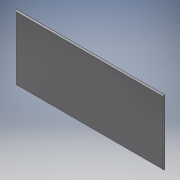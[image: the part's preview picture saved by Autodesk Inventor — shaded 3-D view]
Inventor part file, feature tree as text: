
AUTODESK INVENTOR PART (.ipt)
format: ipt  version: 2018 (Build 220112000, 112)  size: 105,472 bytes
history: native  units: in
note: dims shown in document units (in); Inventor stores cm internally (conversion verified against a paired STEP export)
features: other x3, extrude x2, sketch x2, fillet x1, reference x1, projected_geometry x1
ambient origin geometry x8: Origin, YZ Plane, XZ Plane, XY Plane, X Axis, Y Axis, Z Axis, Center Point
bodies: Solid1 (feature_tree)
feature tree (10):
  extrude  "Extrusion1"  Depth=0.005in TaperAngle=0.0deg
  extrude  "Extrusion2"  [1 undecoded]
  fillet  "Fillet1"  [1 undecoded]
  sketch  "Sketch1"  dims[d0=0.001in d1=0.0in d2=0.005in d3=0.0in]
  reference  "Reference1"
  sketch  "Sketch2"  dims[d4=0.005in]
  projected_geometry  "Projected Loop1"
  other  "<userpath>\Documents\Commodore Cube Project\Case\Assembly.iam"
  other  "Assembly.iam"
  other  "Dome:1"
note: 2 required parameter values undecoded (feature->parameter linkage not recoverable at this tier; creation-order binding heuristic only, values carry confidence <= 0.55)
